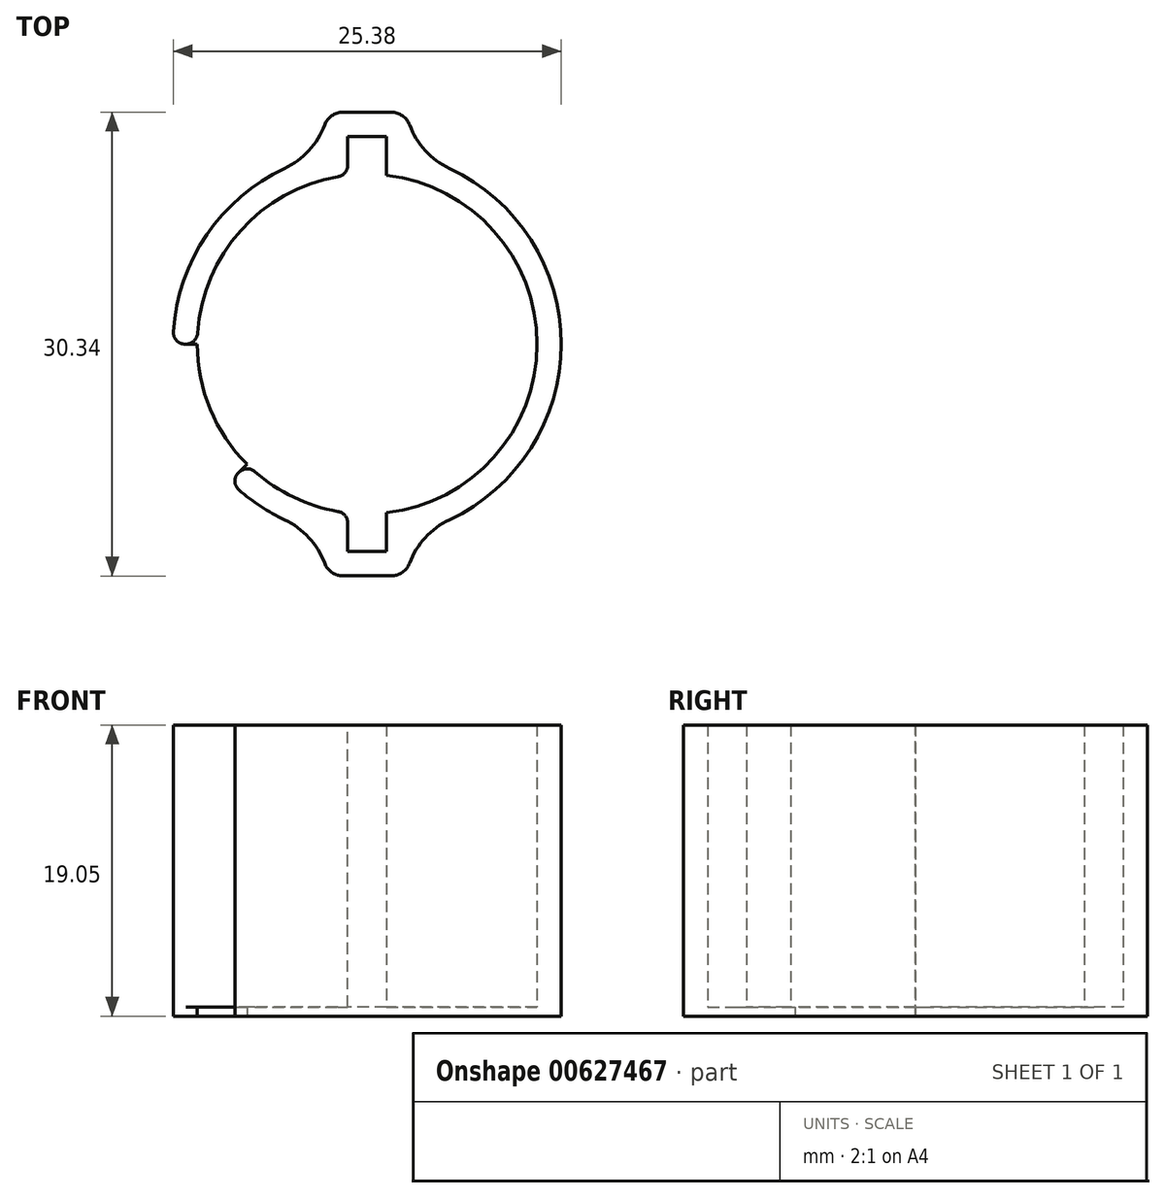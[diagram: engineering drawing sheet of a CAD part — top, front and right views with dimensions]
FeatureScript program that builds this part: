
annotation { "Feature Type Name" : "Feature", "Feature Type Description" : "" }
export const myFeature = defineFeature(function(context is Context, id is Id, definition is map)
    precondition{}
    {
        {
            var Q0;
            Q0=qCreatedBy(makeId("Top.planeOp"),FACE);
            var sketch = newSketch(context, id + "F0", { "sketchPlane" : qUnion([Q0])});
            skArc(sketch, "E0", {"start": v(-1.27, 11.04) * mm, "mid": v(-11.11, 0) * mm, "end": v(-1.27, -11.04) * mm});
            skLineSegment(sketch, "E1", {"start": v(0, 13.58) * mm, "end": v(1.27, 13.58) * mm});
            skLineSegment(sketch, "E2", {"start": v(1.27, 13.58) * mm, "end": v(1.27, 11.04) * mm});
            skLineSegment(sketch, "E3", {"start": v(0, 13.58) * mm, "end": v(-1.27, 13.58) * mm});
            skLineSegment(sketch, "E4", {"start": v(-1.27, 13.58) * mm, "end": v(-1.27, 11.04) * mm});
            skPoint(sketch, "E5.endSnap0", {"position": v(0, -11.11) * mm});
            skLineSegment(sketch, "E6", {"start": v(0, -13.58) * mm, "end": v(1.27, -13.58) * mm});
            skLineSegment(sketch, "E7", {"start": v(1.27, -13.58) * mm, "end": v(1.27, -11.04) * mm});
            skLineSegment(sketch, "E8", {"start": v(0, -13.58) * mm, "end": v(-1.27, -13.58) * mm});
            skLineSegment(sketch, "E9", {"start": v(-1.27, -13.58) * mm, "end": v(-1.27, -11.04) * mm});
            skArc(sketch, "E10.trimOffspring", {"start": v(1.27, -11.04) * mm, "mid": v(11.11, 0) * mm, "end": v(1.27, 11.04) * mm});
            skLineSegment(sketch, "E11.0", {"start": v(0, 15.17) * mm, "end": v(-2.86, 15.17) * mm});
            skLineSegment(sketch, "E11.1", {"start": v(-2.86, 15.17) * mm, "end": v(-2.86, 12.37) * mm});
            skLineSegment(sketch, "E11.2", {"start": v(0, 15.17) * mm, "end": v(2.86, 15.17) * mm});
            skArc(sketch, "E11.3", {"start": v(-2.86, 12.37) * mm, "mid": v(-12.7, 0) * mm, "end": v(-2.86, -12.37) * mm});
            skLineSegment(sketch, "E11.4", {"start": v(-2.86, -15.17) * mm, "end": v(-2.86, -12.37) * mm});
            skLineSegment(sketch, "E11.5", {"start": v(0, -15.17) * mm, "end": v(-2.86, -15.17) * mm});
            skLineSegment(sketch, "E11.6", {"start": v(2.86, 15.17) * mm, "end": v(2.86, 12.37) * mm});
            skArc(sketch, "E11.7", {"start": v(2.86, -12.37) * mm, "mid": v(12.7, 0) * mm, "end": v(2.86, 12.37) * mm});
            skLineSegment(sketch, "E11.8", {"start": v(2.86, -15.17) * mm, "end": v(2.86, -12.37) * mm});
            skLineSegment(sketch, "E11.9", {"start": v(0, -15.17) * mm, "end": v(2.86, -15.17) * mm});
            skLineSegment(sketch, "E12", {"start": v(-11.11, 0) * mm, "end": v(-12.7, 0) * mm});
            skPoint(sketch, "E12.endSnap0", {"position": v(-12.7, 0) * mm});
            skLineSegment(sketch, "E13", {"start": v(-12.7, 0) * mm, "end": v(-11.11, 0) * mm});
            skLineSegment(sketch, "E14", {"start": v(-7.86, -7.86) * mm, "end": v(-8.98, -8.98) * mm});
            skPoint(sketch, "E15.orphan", {"position": v(-34.97, 0) * mm});
            skSolve(sketch);
        }
        {
            var Q0;
            Q0=makeQuery(id+"F0.imprint","IMPRINT",FACE,{"disambiguationData":[TD([[makeQuery(id+"F0.imprint","IMPRINT",EDGE,{"derivedFrom":sQuery(id+"F0.wireOp",EDGE,"E0")}),1.0]])]});
            var Q1;
            {var subQ0=sQuery(id+"F0.wireOp",EDGE,"E13");Q1=makeQuery(id+"F0.imprint","IMPRINT",FACE,{"disambiguationData":[TD([[makeQuery(id+"F0.imprint","IMPRINT",EDGE,{"derivedFrom":subQ0}),-1.0]])]});}
            extrude(context, id + "F1", {"entities" : qUnion([Q0, Q1]), "depth" : 0.6 * mm, "offsetDistance" : 25.4 * mm});
        }
        {
            var Q0;
            Q0=makeQuery(id+"F0.imprint","IMPRINT",FACE,{"disambiguationData":[TD([[makeQuery(id+"F0.imprint","IMPRINT",EDGE,{"derivedFrom":sQuery(id+"F0.wireOp",EDGE,"E1")}),1.0]])]});
            extrude(context, id + "F2", {"entities" : qUnion([Q0]), "operationType" : NewBodyOperationType.ADD, "depth" : 19.05 * mm, "offsetDistance" : 25.4 * mm});
        }
        {
            var Q0;
            Q0=makeQuery(id+"F2.opExtrude","SWEPT_EDGE",EDGE,{"disambiguationData":[OSD([sQuery(id+"F0.wireOp",EDGE,"E11.8"),sQuery(id+"F0.wireOp",EDGE,"E11.9")])]});
            var Q1;
            Q1=makeQuery(id+"F2.opExtrude","SWEPT_EDGE",EDGE,{"disambiguationData":[OSD([sQuery(id+"F0.wireOp",EDGE,"E11.4"),sQuery(id+"F0.wireOp",EDGE,"E11.5")])]});
            var Q2;
            Q2=makeQuery(id+"F2.opExtrude","SWEPT_EDGE",EDGE,{"disambiguationData":[OSD([sQuery(id+"F0.wireOp",EDGE,"E11.0"),sQuery(id+"F0.wireOp",EDGE,"E11.1")])]});
            var Q3;
            Q3=makeQuery(id+"F2.opExtrude","SWEPT_EDGE",EDGE,{"disambiguationData":[OSD([sQuery(id+"F0.wireOp",EDGE,"E11.2"),sQuery(id+"F0.wireOp",EDGE,"E11.6")])]});
            fillet(context, id + "F3", {"entities" : qUnion([Q0, Q1, Q2, Q3]), "radius" : 1.27 * mm, "tangentPropagation" : true, "allowEdgeOverflow" : false});
        }
        {
            var Q0;
            Q0=makeQuery(id+"F2.opExtrude","SWEPT_EDGE",EDGE,{"disambiguationData":[OSD([sQuery(id+"F0.wireOp",EDGE,"E11.6"),sQuery(id+"F0.wireOp",EDGE,"E11.7")])]});
            var Q1;
            Q1=makeQuery(id+"F2.opExtrude","SWEPT_EDGE",EDGE,{"disambiguationData":[OSD([sQuery(id+"F0.wireOp",EDGE,"E11.1"),sQuery(id+"F0.wireOp",EDGE,"E11.3")])]});
            var Q2;
            Q2=makeQuery(id+"F2.opExtrude","SWEPT_EDGE",EDGE,{"disambiguationData":[OSD([sQuery(id+"F0.wireOp",EDGE,"E11.3"),sQuery(id+"F0.wireOp",EDGE,"E11.4")])]});
            var Q3;
            Q3=makeQuery(id+"F2.opExtrude","SWEPT_EDGE",EDGE,{"disambiguationData":[OSD([sQuery(id+"F0.wireOp",EDGE,"E11.7"),sQuery(id+"F0.wireOp",EDGE,"E11.8")])]});
            fillet(context, id + "F4", {"entities" : qUnion([Q0, Q1, Q2, Q3]), "radius" : 5.08 * mm, "tangentPropagation" : true, "allowEdgeOverflow" : false});
        }
        {
            var Q0;
            Q0=makeQuery(id+"F2.opExtrude","SWEPT_EDGE",EDGE,{"disambiguationData":[OSD([sQuery(id+"F0.wireOp",EDGE,"E11.3"),sQuery(id+"F0.wireOp",EDGE,"E13")])]});
            var Q1;
            Q1=makeQuery(id+"F2.opExtrude","SWEPT_EDGE",EDGE,{"disambiguationData":[OSD([sQuery(id+"F0.wireOp",EDGE,"E0"),sQuery(id+"F0.wireOp",EDGE,"E13")])]});
            var Q2;
            Q2=makeQuery(id+"F2.opExtrude","SWEPT_EDGE",EDGE,{"disambiguationData":[OSD([sQuery(id+"F0.wireOp",EDGE,"E0"),sQuery(id+"F0.wireOp",EDGE,"E14")])]});
            var Q3;
            Q3=makeQuery(id+"F2.opExtrude","SWEPT_EDGE",EDGE,{"disambiguationData":[OSD([sQuery(id+"F0.wireOp",EDGE,"E11.3"),sQuery(id+"F0.wireOp",EDGE,"E14")])]});
            fillet(context, id + "F5", {"entities" : qUnion([Q0, Q1, Q2, Q3]), "radius" : 0.76 * mm, "tangentPropagation" : true, "allowEdgeOverflow" : false});
        }
    });
